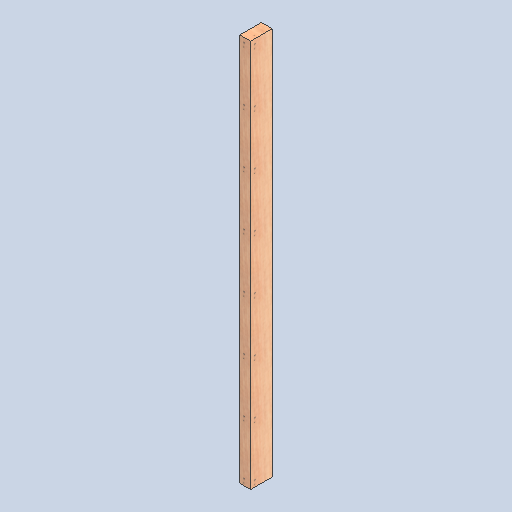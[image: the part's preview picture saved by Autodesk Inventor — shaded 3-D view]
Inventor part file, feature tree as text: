
AUTODESK INVENTOR PART (.ipt)
format: ipt  version: 2025 (Build 290162000, 162)  size: 146,944 bytes
history: native  units: in
note: dims shown in document units (in); Inventor stores cm internally (conversion verified against a paired STEP export)
features: extrude x1, sketch x1
ambient origin geometry x8: Origin, YZ Plane, XZ Plane, XY Plane, X Axis, Y Axis, Z Axis, Center Point
bodies: Solid1 (feature_tree)
feature tree (2):
  extrude  "Extrusion1"  Depth=4.0in
  sketch  "Sketch1"  dims[d0=2.0in d1=4.0in d2=72.0in d3=0.0in d5=0.5in d6=0.0344in d7=0.5in d8=0.0344in]
